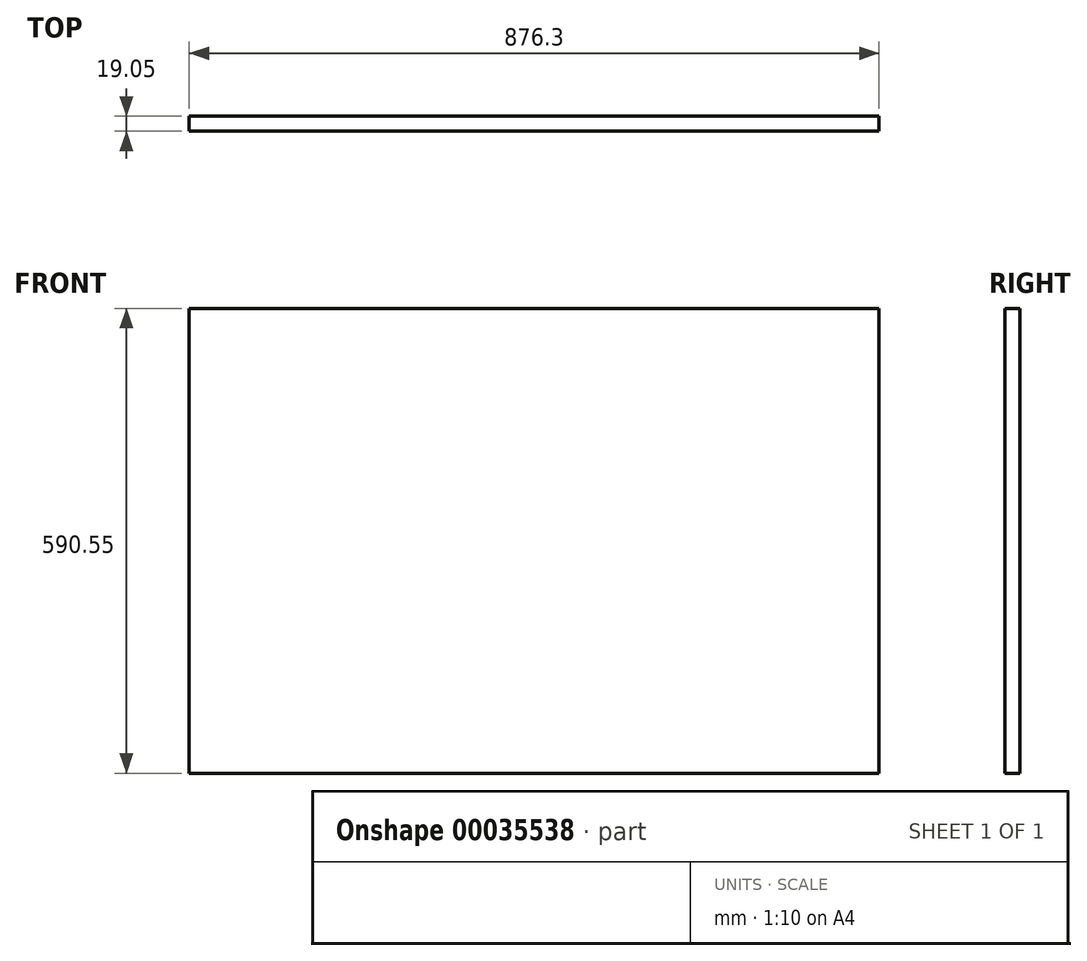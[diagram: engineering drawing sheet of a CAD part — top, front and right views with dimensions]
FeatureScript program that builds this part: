
annotation { "Feature Type Name" : "Feature", "Feature Type Description" : "" }
export const myFeature = defineFeature(function(context is Context, id is Id, definition is map)
    precondition{}
    {
        {
            var Q0;
            Q0=qCreatedBy(makeId("Front.planeOp"),FACE);
            var sketch = newSketch(context, id + "F0", { "sketchPlane" : qUnion([Q0])});
            skLineSegment(sketch, "E0.bottom", {"start": v(-437.31, 376.6) * mm, "end": v(438.99, 376.6) * mm});
            skLineSegment(sketch, "E0.top", {"start": v(-437.31, -213.96) * mm, "end": v(438.99, -213.96) * mm});
            skLineSegment(sketch, "E0.left", {"start": v(-437.31, 376.6) * mm, "end": v(-437.31, -213.96) * mm});
            skLineSegment(sketch, "E0.right", {"start": v(438.99, 376.6) * mm, "end": v(438.99, -213.96) * mm});
            skSolve(sketch);
        }
        {
            var Q0;
            Q0 = qSketchRegion(id + "F0", true);
            extrude(context, id + "F1", {"entities" : qUnion([Q0]), "depth" : 19.05 * mm});
        }
    });
